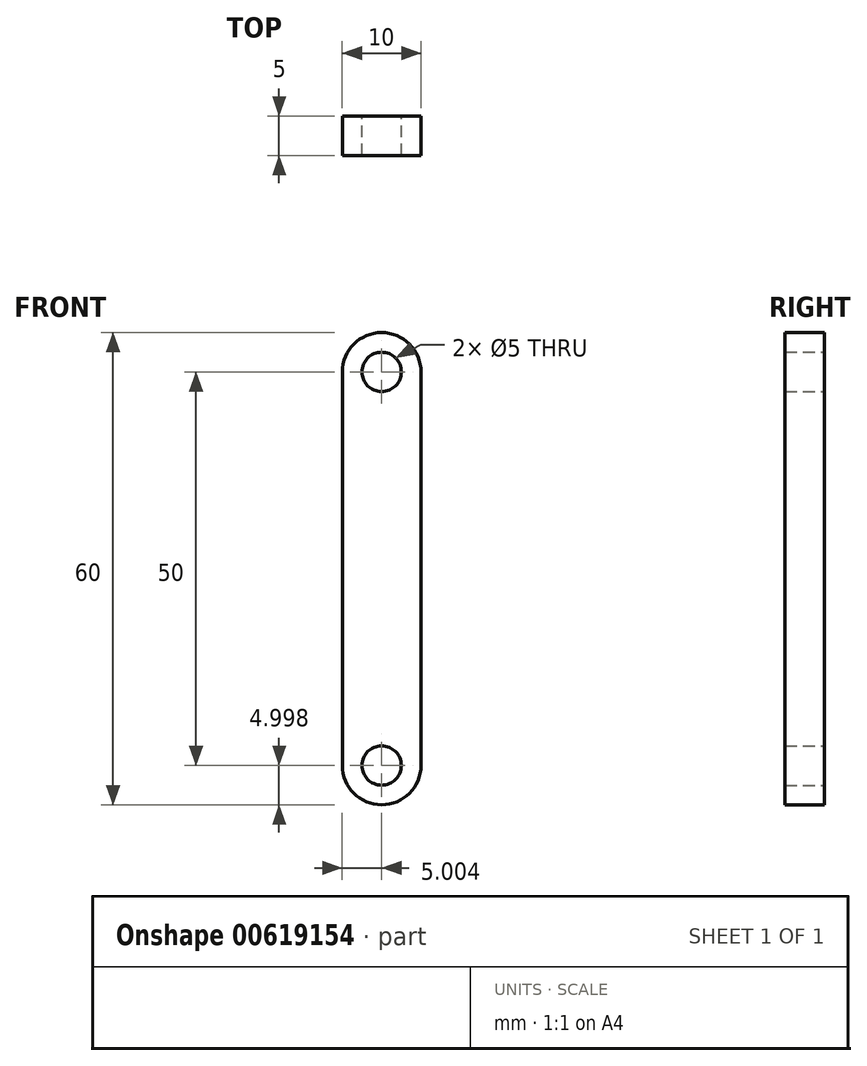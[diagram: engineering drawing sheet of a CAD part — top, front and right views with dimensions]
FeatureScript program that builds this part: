
annotation { "Feature Type Name" : "Feature", "Feature Type Description" : "" }
export const myFeature = defineFeature(function(context is Context, id is Id, definition is map)
    precondition{}
    {
        {
            var Q0;
            Q0=qCreatedBy(makeId("Front.planeOp"),FACE);
            var sketch = newSketch(context, id + "F0", { "sketchPlane" : qUnion([Q0])});
            skLineSegment(sketch, "E0", {"start": v(-19.96, 32.1) * mm, "end": v(-19.96, -17.9) * mm});
            skArc(sketch, "E1", {"start": v(-19.96, -17.9) * mm, "mid": v(-14.96, -22.9) * mm, "end": v(-9.96, -17.9) * mm});
            skLineSegment(sketch, "E2", {"start": v(-9.96, -17.9) * mm, "end": v(-9.96, 32.1) * mm});
            skArc(sketch, "E3", {"start": v(-19.96, 32.1) * mm, "mid": v(-14.96, 37.1) * mm, "end": v(-9.96, 32.1) * mm});
            skCircle(sketch, "E4", {"center": v(-14.96, 32.1) * mm, "radius": 2.5 * mm});
            skCircle(sketch, "E5", {"center": v(-14.96, -17.9) * mm, "radius": 2.5 * mm});
            skSolve(sketch);
        }
        {
            var Q0;
            Q0 = qSketchRegion(id + "F0", true);
            extrude(context, id + "F1", {"entities" : qUnion([Q0]), "depth" : 5 * mm, "offsetDistance" : 25 * mm});
        }
    });
